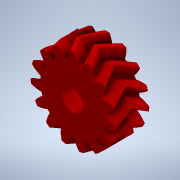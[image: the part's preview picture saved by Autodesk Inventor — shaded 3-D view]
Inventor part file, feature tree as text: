
AUTODESK INVENTOR PART (.ipt)
format: ipt  version: 2020 (Build 240168000, 168)  size: 583,680 bytes
history: native  units: mm (DEFAULTED — no unit token found)
features: extrude x3, plane x3, other x3, sketch x3, mirror x1
ambient origin geometry x8: Origin, YZ Plane, XZ Plane, XY Plane, X Axis, Y Axis, Z Axis, Center Point
bodies: Solid1 (feature_tree)
feature tree (13):
  extrude  "Extrusion1"  Depth=5.0mm TaperAngle=0.0deg
  plane  "Work Plane2"
  plane  "Work Plane8"
  plane  "Work Plane9"
  other  "Spur Gear"
  mirror  "Mirror1"
  sketch  "Sketch3"  dims[d16=21.6mm d17=0.0mm d34=2.094395mm d39=0.0mm d41=0.0mm d43=21.6mm d46=21.6mm d47=0.0mm d48=0.0mm d49=6.0mm d50=10.0mm d51=0.0mm d52=3.0mm d53=3.0mm d54=3.0mm d55=3.0mm d57=14.0mm d58=6.0mm d59=0.0mm]
  extrude  "Extrusion2"  Depth=10.0mm TaperAngle=0.0deg
  extrude  "Extrusion3"  Depth=6.0mm TaperAngle=0.0deg
  sketch  "Sketch1"  dims[d0=24.099662mm d1=5.0mm d2=0.0mm]
  sketch  "Sketch2"  dims[d3=21.6mm d4=10.0mm d5=0.0mm]
  other  "Srf1"
  other  "Pitch Diameter"
